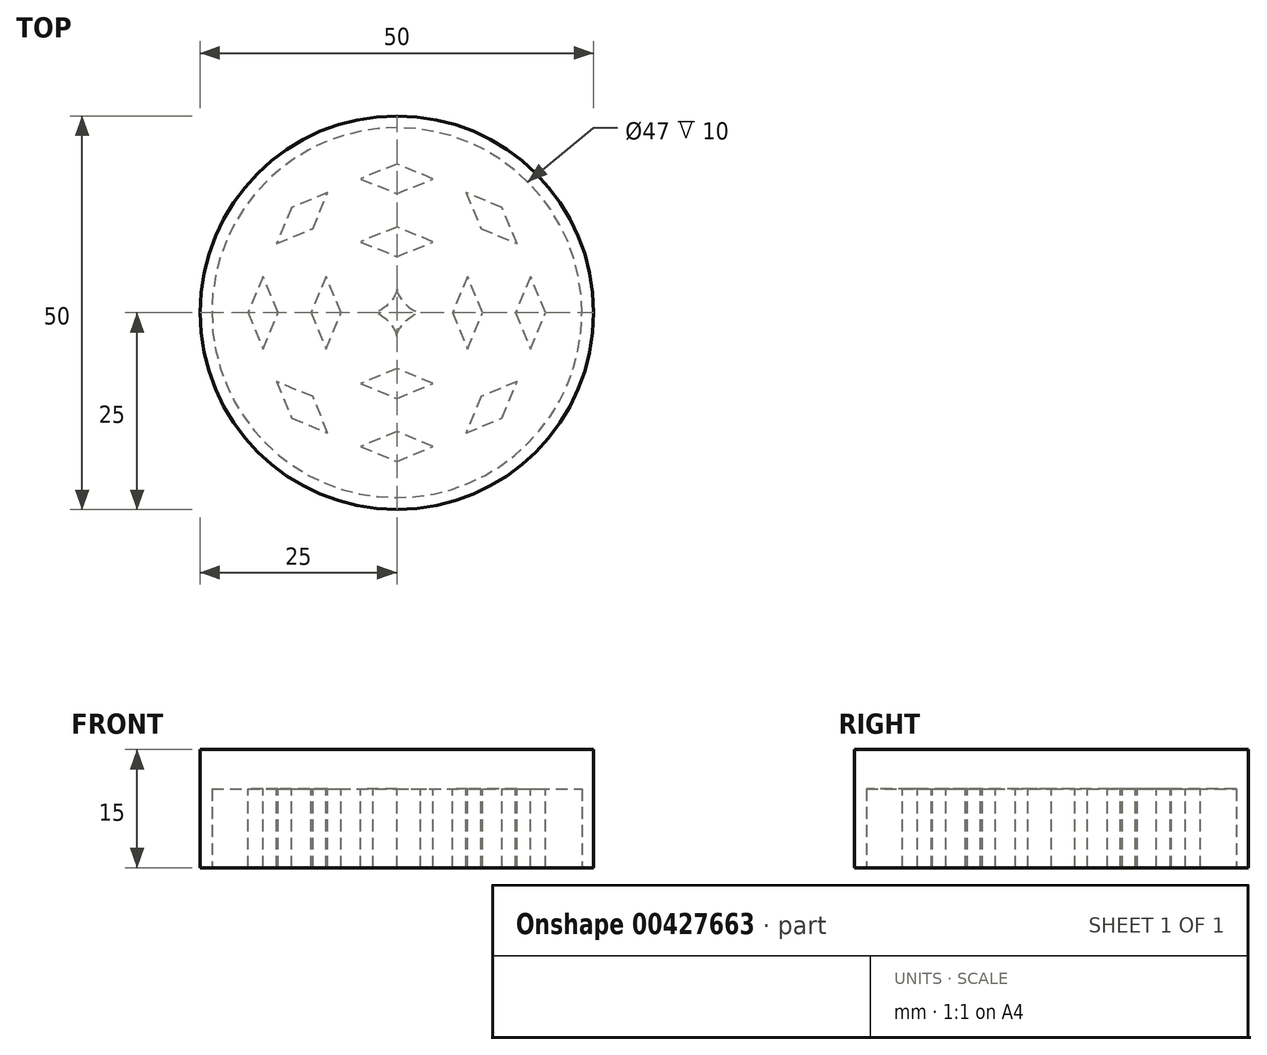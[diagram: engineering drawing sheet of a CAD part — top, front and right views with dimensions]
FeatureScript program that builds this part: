
annotation { "Feature Type Name" : "Feature", "Feature Type Description" : "" }
export const myFeature = defineFeature(function(context is Context, id is Id, definition is map)
    precondition{}
    {
        {
            var Q0;
            Q0=qCreatedBy(makeId("Top.planeOp"),FACE);
            var sketch = newSketch(context, id + "F0", { "sketchPlane" : qUnion([Q0])});
            skCircle(sketch, "E0", {"center": v(0, 0) * mm, "radius": 25 * mm});
            skSolve(sketch);
        }
        {
            var Q0;
            Q0=makeQuery(id+"F0.imprint","IMPRINT",FACE,{"disambiguationData":[TD([[makeQuery(id+"F0.imprint","IMPRINT",EDGE,{"derivedFrom":sQuery(id+"F0.wireOp",EDGE,"E0")}),1.0]])]});
            extrude(context, id + "F1", {"entities" : qUnion([Q0]), "depth" : 15 * mm});
        }
        {
            var Q0;
            Q0=makeQuery(id+"F1.opExtrude","CAP_FACE",FACE,{"disambiguationData":[OSD([sQuery(id+"F0.wireOp",EDGE,"E0")])],"isStart":true});
            var sketch = newSketch(context, id + "F2", { "sketchPlane" : qUnion([Q0])});
            skCircle(sketch, "E1", {"center": v(0, 0) * mm, "radius": 23.5 * mm});
            skSolve(sketch);
        }
        {
            var Q0;
            Q0=makeQuery(id+"F2.imprint","IMPRINT",FACE,{"disambiguationData":[TD([[makeQuery(id+"F2.imprint","IMPRINT",EDGE,{"derivedFrom":sQuery(id+"F2.wireOp",EDGE,"E1")}),1.0]])]});
            extrude(context, id + "F3", {"entities" : qUnion([Q0]), "operationType" : NewBodyOperationType.REMOVE, "oppositeDirection" : true, "depth" : 10 * mm});
        }
        {
            var Q0;
            Q0=makeQuery(id+"F3.boolean.opBoolean","COPY",FACE,{"derivedFrom":makeQuery(id+"F3.opExtrude","CAP_FACE",FACE,{"disambiguationData":[OSD([sQuery(id+"F2.wireOp",EDGE,"E1")])],"isStart":false})});
            var sketch = newSketch(context, id + "F4", { "sketchPlane" : qUnion([Q0])});
            skCircle(sketch, "E2", {"center": v(0, 0) * mm, "radius": 3 * mm, "construction": true});
            skCircle(sketch, "E3", {"center": v(0, 0) * mm, "radius": 7 * mm, "construction": true});
            skCircle(sketch, "E4", {"center": v(0, 0) * mm, "radius": 11 * mm, "construction": true});
            skCircle(sketch, "E5", {"center": v(0, 0) * mm, "radius": 15 * mm, "construction": true});
            skFitSpline(sketch, "E6", {"points": [v(0, 3) * mm, v(-3, 0) * mm], "startDerivative": vector(0, -3.17) * mm, "endDerivative": vector(-3.28, 0) * mm});
            skFitSpline(sketch, "E7.MirrorCS", {"points": [v(0, 3) * mm, v(3, 0) * mm], "startDerivative": vector(0, -3.17) * mm, "endDerivative": vector(3.28, 0) * mm});
            skFitSpline(sketch, "E8.MirrorCS", {"points": [v(0, -3) * mm, v(3, 0) * mm], "startDerivative": vector(0, 3.17) * mm, "endDerivative": vector(3.28, 0) * mm});
            skFitSpline(sketch, "E9.MirrorCS", {"points": [v(0, -3) * mm, v(-3, 0) * mm], "startDerivative": vector(0, 3.17) * mm, "endDerivative": vector(-3.28, 0) * mm});
            skCircle(sketch, "E10", {"center": v(0, 0) * mm, "radius": 19 * mm, "construction": true});
            skSolve(sketch);
        }
        {
            var Q0;
            {var subQ1=sQuery(id+"F4.wireOp",EDGE,"E6");Q0=makeQuery(id+"F4.imprint","IMPRINT",FACE,{"disambiguationData":[TD([[makeQuery(id+"F4.imprint","IMPRINT",EDGE,{"derivedFrom":subQ1}),-1.0]])]});}
            var sketch = newSketch(context, id + "F5", { "sketchPlane" : qUnion([Q0])});
            skLineSegment(sketch, "E11", {"start": v(4.59, -9) * mm, "end": v(0, -10.9) * mm});
            skLineSegment(sketch, "E12", {"start": v(0, -10.9) * mm, "end": v(-4.59, -9) * mm});
            skLineSegment(sketch, "E13", {"start": v(-4.59, -9) * mm, "end": v(0, -7.1) * mm});
            skLineSegment(sketch, "E14", {"start": v(0, -7.1) * mm, "end": v(4.59, -9) * mm});
            skPoint(sketch, "E15", {"position": v(0, -7) * mm});
            skLineSegment(sketch, "E16.1.0", {"start": v(9, -4.59) * mm, "end": v(7.1, 0) * mm});
            skLineSegment(sketch, "E16.1.1", {"start": v(7.1, 0) * mm, "end": v(9, 4.59) * mm});
            skLineSegment(sketch, "E16.1.2", {"start": v(9, 4.59) * mm, "end": v(10.9, 0) * mm});
            skLineSegment(sketch, "E16.1.3", {"start": v(10.9, 0) * mm, "end": v(9, -4.59) * mm});
            skLineSegment(sketch, "E16.2.0", {"start": v(4.59, 9) * mm, "end": v(0, 7.1) * mm});
            skLineSegment(sketch, "E16.2.1", {"start": v(0, 7.1) * mm, "end": v(-4.59, 9) * mm});
            skLineSegment(sketch, "E16.2.2", {"start": v(-4.59, 9) * mm, "end": v(0, 10.9) * mm});
            skLineSegment(sketch, "E16.2.3", {"start": v(0, 10.9) * mm, "end": v(4.59, 9) * mm});
            skLineSegment(sketch, "E16.3.0", {"start": v(-9, 4.59) * mm, "end": v(-7.1, 0) * mm});
            skLineSegment(sketch, "E16.3.1", {"start": v(-7.1, 0) * mm, "end": v(-9, -4.59) * mm});
            skLineSegment(sketch, "E16.3.2", {"start": v(-9, -4.59) * mm, "end": v(-10.9, 0) * mm});
            skLineSegment(sketch, "E16.3.3", {"start": v(-10.9, 0) * mm, "end": v(-9, 4.59) * mm});
            skPoint(sketch, "E16.center", {"position": v(0, 0) * mm});
            skLineSegment(sketch, "E17.2.0", {"start": v(4.59, 17) * mm, "end": v(0, 15.1) * mm});
            skLineSegment(sketch, "E17.2.1", {"start": v(0, 15.1) * mm, "end": v(-4.59, 17) * mm});
            skLineSegment(sketch, "E17.2.2", {"start": v(-4.59, 17) * mm, "end": v(0, 18.9) * mm});
            skLineSegment(sketch, "E17.2.3", {"start": v(0, 18.9) * mm, "end": v(4.59, 17) * mm});
            skPoint(sketch, "E18", {"position": v(0, 15) * mm});
            skLineSegment(sketch, "E19.1.0", {"start": v(-10.68, 10.68) * mm, "end": v(-15.26, 8.78) * mm});
            skLineSegment(sketch, "E19.1.1", {"start": v(-15.26, 8.78) * mm, "end": v(-13.36, 13.36) * mm});
            skLineSegment(sketch, "E19.1.2", {"start": v(-13.36, 13.36) * mm, "end": v(-8.78, 15.26) * mm});
            skLineSegment(sketch, "E19.1.3", {"start": v(-8.78, 15.26) * mm, "end": v(-10.68, 10.68) * mm});
            skLineSegment(sketch, "E19.2.0", {"start": v(-15.1, 0) * mm, "end": v(-17, -4.59) * mm});
            skLineSegment(sketch, "E19.2.1", {"start": v(-17, -4.59) * mm, "end": v(-18.9, 0) * mm});
            skLineSegment(sketch, "E19.2.2", {"start": v(-18.9, 0) * mm, "end": v(-17, 4.59) * mm});
            skLineSegment(sketch, "E19.2.3", {"start": v(-17, 4.59) * mm, "end": v(-15.1, 0) * mm});
            skLineSegment(sketch, "E19.3.0", {"start": v(-10.68, -10.68) * mm, "end": v(-8.78, -15.26) * mm});
            skLineSegment(sketch, "E19.3.1", {"start": v(-8.78, -15.26) * mm, "end": v(-13.36, -13.36) * mm});
            skLineSegment(sketch, "E19.3.2", {"start": v(-13.36, -13.36) * mm, "end": v(-15.26, -8.78) * mm});
            skLineSegment(sketch, "E19.3.3", {"start": v(-15.26, -8.78) * mm, "end": v(-10.68, -10.68) * mm});
            skLineSegment(sketch, "E19.4.0", {"start": v(0, -15.1) * mm, "end": v(4.59, -17) * mm});
            skLineSegment(sketch, "E19.4.1", {"start": v(4.59, -17) * mm, "end": v(0, -18.9) * mm});
            skLineSegment(sketch, "E19.4.2", {"start": v(0, -18.9) * mm, "end": v(-4.59, -17) * mm});
            skLineSegment(sketch, "E19.4.3", {"start": v(-4.59, -17) * mm, "end": v(0, -15.1) * mm});
            skLineSegment(sketch, "E19.5.0", {"start": v(10.68, -10.68) * mm, "end": v(15.26, -8.78) * mm});
            skLineSegment(sketch, "E19.5.1", {"start": v(15.26, -8.78) * mm, "end": v(13.36, -13.36) * mm});
            skLineSegment(sketch, "E19.5.2", {"start": v(13.36, -13.36) * mm, "end": v(8.78, -15.26) * mm});
            skLineSegment(sketch, "E19.5.3", {"start": v(8.78, -15.26) * mm, "end": v(10.68, -10.68) * mm});
            skLineSegment(sketch, "E19.6.0", {"start": v(15.1, 0) * mm, "end": v(17, 4.59) * mm});
            skLineSegment(sketch, "E19.6.1", {"start": v(17, 4.59) * mm, "end": v(18.9, 0) * mm});
            skLineSegment(sketch, "E19.6.2", {"start": v(18.9, 0) * mm, "end": v(17, -4.59) * mm});
            skLineSegment(sketch, "E19.6.3", {"start": v(17, -4.59) * mm, "end": v(15.1, 0) * mm});
            skLineSegment(sketch, "E19.7.0", {"start": v(10.68, 10.68) * mm, "end": v(8.78, 15.26) * mm});
            skLineSegment(sketch, "E19.7.1", {"start": v(8.78, 15.26) * mm, "end": v(13.36, 13.36) * mm});
            skLineSegment(sketch, "E19.7.2", {"start": v(13.36, 13.36) * mm, "end": v(15.26, 8.78) * mm});
            skLineSegment(sketch, "E19.7.3", {"start": v(15.26, 8.78) * mm, "end": v(10.68, 10.68) * mm});
            skSolve(sketch);
        }
        {
            var Q0;
            Q0 = qSketchRegion(id + "F5", true);
            extrude(context, id + "F6", {"entities" : qUnion([Q0]), "operationType" : NewBodyOperationType.ADD, "depth" : 10 * mm});
        }
        {
            var Q0;
            {var subQ0=sQuery(id+"F4.wireOp",EDGE,"E6");Q0=makeQuery(id+"F4.imprint","IMPRINT",FACE,{"disambiguationData":[TD([[makeQuery(id+"F4.imprint","IMPRINT",EDGE,{"derivedFrom":subQ0}),1.0]])]});}
            extrude(context, id + "F7", {"entities" : qUnion([Q0]), "operationType" : NewBodyOperationType.ADD, "depth" : 10 * mm});
        }
    });
